# Revit family: Keilhauer_Pact_Bench_77103
name_source: partatom
category: Furniture
revit_build: Autodesk Revit 2017 (Build: 20160225_1515(x64)
units: mm (PartAtom-declared; Revit-internal decimal feet)

## family parameters
Always vertical = Yes
Cut with Voids When Loaded = No
OmniClass Number = 23.40.70.14.64.11
OmniClass Title = Office Furniture
Room Calculation Point = No
Shared = No
Work Plane-Based = No

## types (8) — shared parameters
Assembly Code = E2020200
Catalog = Pact
Manufacturer = Keilhauer, Corp.
Product Documentation Link = http://www.keilhauer.com
URL = http://www.keilhauer.com

## per-type parameters (varying)
| type | Description | Left | Length 1 | Length 2 | Model | Right | Type |
| 84" bench raf arm | Pact 84" half back bench with RAF arm | Yes | 1031.443 mm | 861.02 mm | 77133 | No | 8 |
| 72" bench raf arm | Pact 72" half back bench with RAF arm | Yes | 872.693 mm | 567.62 mm | 77123 | No | 7 |
| 57" bench raf arm | Pact 57" half back bench with RAF arm | Yes | 682.193 mm | 186.62 mm | 77113 | No | 6 |
| 32" bench raf arm | Pact 32" half back bench with RAF arm | Yes | 364.693 mm | 186.62 mm | 77103 | No | 5 |
| 84" bench laf arm | Pact 84" half back bench with LAF arm | No | 1031.443 mm | 861.02 mm | 77132 | Yes | 4 |
| 72" bench laf arm | Pact 72" half back bench with LAF arm | No | 872.693 mm | 567.62 mm | 77122 | Yes | 3 |
| 57" bench laf arm | Pact 57" half back bench with LAF arm | No | 682.193 mm | 186.62 mm | 77112 | Yes | 2 |
| 32" bench laf arm | Pact 32" half back bench with LAF arm | No | 364.693 mm | 186.62 mm | 77102 | Yes | 1 |

## geometry (parser evidence)
native form markers: Sweep x2
no freeform markers — native parametric forms only
